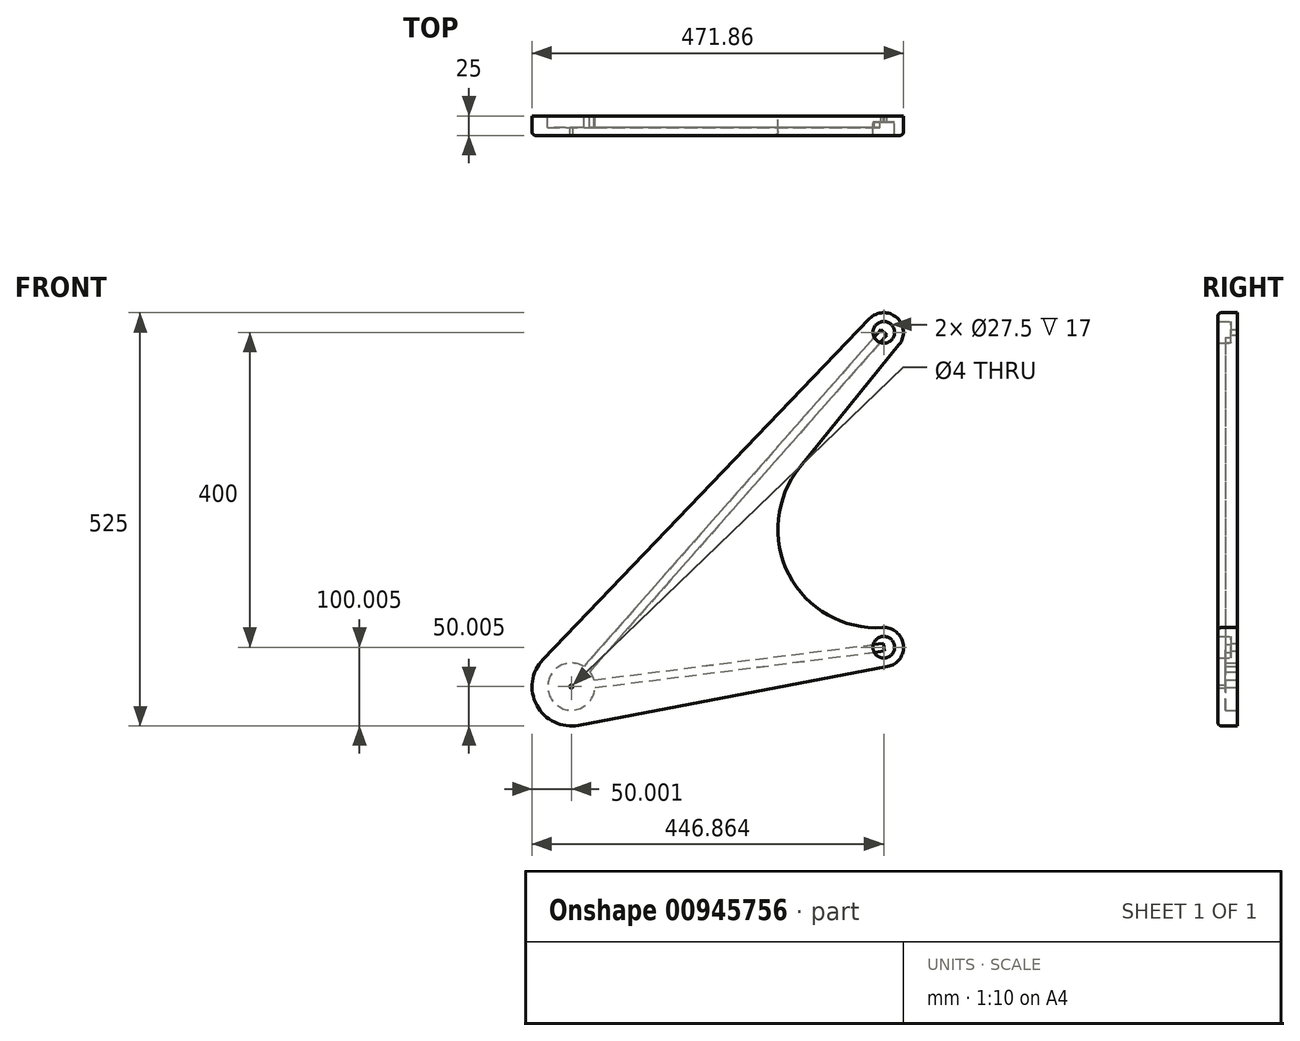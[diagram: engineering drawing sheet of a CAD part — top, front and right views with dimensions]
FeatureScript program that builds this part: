
annotation { "Feature Type Name" : "Feature", "Feature Type Description" : "" }
export const myFeature = defineFeature(function(context is Context, id is Id, definition is map)
    precondition{}
    {
        {
            var Q0;
            Q0=qCreatedBy(makeId("Front.planeOp"),FACE);
            var sketch = newSketch(context, id + "F0", { "sketchPlane" : qUnion([Q0])});
            skLineSegment(sketch, "E0", {"start": v(27.48, 326.53) * mm, "end": v(-369.38, -123.47) * mm});
            skLineSegment(sketch, "E1", {"start": v(-369.38, -123.47) * mm, "end": v(27.48, -73.47) * mm});
            skLineSegment(sketch, "E2", {"start": v(27.48, -73.47) * mm, "end": v(27.48, 326.53) * mm});
            skCircle(sketch, "E3", {"center": v(-369.38, -123.47) * mm, "radius": 50 * mm});
            skCircle(sketch, "E4", {"center": v(-369.38, -123.47) * mm, "radius": 30 * mm});
            skCircle(sketch, "E5", {"center": v(27.48, -73.47) * mm, "radius": 13.75 * mm});
            skCircle(sketch, "E6", {"center": v(27.48, 326.53) * mm, "radius": 13.75 * mm});
            skCircle(sketch, "E7", {"center": v(27.48, 326.53) * mm, "radius": 25 * mm});
            skCircle(sketch, "E8", {"center": v(27.48, -73.47) * mm, "radius": 25 * mm});
            skLineSegment(sketch, "E9", {"start": v(-405.47, -88.86) * mm, "end": v(9.44, 343.84) * mm});
            skLineSegment(sketch, "E10", {"start": v(-360.04, -172.59) * mm, "end": v(32.15, -98.03) * mm});
            skLineSegment(sketch, "E11", {"start": v(-330.53, -154.95) * mm, "end": v(46.9, 310.8) * mm});
            skLineSegment(sketch, "E12", {"start": v(25.92, -48.51) * mm, "end": v(-372.52, -73.56) * mm});
            skArc(sketch, "E13", {"start": v(25.92, -48.51) * mm, "mid": v(129.3, 133.79) * mm, "end": v(-79.18, 155.2) * mm});
            skCircle(sketch, "E14", {"center": v(18.06, 76.4) * mm, "radius": 125.17 * mm});
            skSolve(sketch);
        }
        {
            var Q0;
            {var subQ0=sQuery(id+"F0.wireOp",EDGE,"E3");var subQ2=sQuery(id+"F0.wireOp",EDGE,"E0");var subQ3=makeQuery(id+"F0.imprint","INTERSECT",VERTEX,{"derivedFrom":[subQ2,subQ0]});Q0=makeQuery(id+"F0.imprint","IMPRINT",FACE,{"disambiguationData":[TD([[makeQuery(id+"F0.imprint","IMPRINT",EDGE,{"disambiguationData":[TD([[subQ3,-1.0]])],"derivedFrom":subQ2}),-1.0]])]});}
            var Q1;
            {var subQ0=sQuery(id+"F0.wireOp",EDGE,"E3");var subQ1=sQuery(id+"F0.wireOp",EDGE,"E0");var subQ2=makeQuery(id+"F0.imprint","INTERSECT",VERTEX,{"derivedFrom":[subQ1,subQ0]});Q1=makeQuery(id+"F0.imprint","IMPRINT",FACE,{"disambiguationData":[TD([[makeQuery(id+"F0.imprint","IMPRINT",EDGE,{"disambiguationData":[TD([[subQ2,-1.0]])],"derivedFrom":subQ1}),1.0]])]});}
            var Q2;
            {var subQ0=sQuery(id+"F0.wireOp",EDGE,"E12");var subQ1=sQuery(id+"F0.wireOp",EDGE,"E0");var subQ2=makeQuery(id+"F0.imprint","INTERSECT",VERTEX,{"derivedFrom":[subQ1,subQ0]});Q2=makeQuery(id+"F0.imprint","IMPRINT",FACE,{"disambiguationData":[TD([[makeQuery(id+"F0.imprint","IMPRINT",EDGE,{"disambiguationData":[TD([[subQ2,-1.0]])],"derivedFrom":subQ1}),-1.0]])]});}
            var Q3;
            {var subQ0=sQuery(id+"F0.wireOp",EDGE,"E9");Q3=makeQuery(id+"F0.imprint","IMPRINT",FACE,{"disambiguationData":[TD([[makeQuery(id+"F0.imprint","IMPRINT",EDGE,{"derivedFrom":subQ0}),-1.0]])]});}
            var Q4;
            {var subQ4=sQuery(id+"F0.wireOp",EDGE,"E7");var subQ5=sQuery(id+"F0.wireOp",EDGE,"E0");var subQ6=makeQuery(id+"F0.imprint","INTERSECT",VERTEX,{"derivedFrom":[subQ5,subQ4]});Q4=makeQuery(id+"F0.imprint","IMPRINT",FACE,{"disambiguationData":[TD([[makeQuery(id+"F0.imprint","IMPRINT",EDGE,{"disambiguationData":[TD([[subQ6,-1.0]])],"derivedFrom":subQ5}),1.0]])]});}
            var Q5;
            {var subQ1=sQuery(id+"F0.wireOp",EDGE,"E0");var subQ7=sQuery(id+"F0.wireOp",EDGE,"E12");var subQ9=makeQuery(id+"F0.imprint","INTERSECT",VERTEX,{"derivedFrom":[subQ1,subQ7]});Q5=makeQuery(id+"F0.imprint","IMPRINT",FACE,{"disambiguationData":[TD([[makeQuery(id+"F0.imprint","IMPRINT",EDGE,{"disambiguationData":[TD([[subQ9,-1.0]])],"derivedFrom":subQ1}),1.0]])]});}
            var Q6;
            {var subQ0=sQuery(id+"F0.wireOp",EDGE,"E12");var subQ1=sQuery(id+"F0.wireOp",EDGE,"E11");var subQ2=makeQuery(id+"F0.imprint","INTERSECT",VERTEX,{"derivedFrom":[subQ1,subQ0]});Q6=makeQuery(id+"F0.imprint","IMPRINT",FACE,{"disambiguationData":[TD([[makeQuery(id+"F0.imprint","IMPRINT",EDGE,{"disambiguationData":[TD([[subQ2,-1.0]])],"derivedFrom":subQ1}),-1.0]])]});}
            var Q7;
            {var subQ1=sQuery(id+"F0.wireOp",EDGE,"E1");var subQ5=sQuery(id+"F0.wireOp",EDGE,"E8");var subQ7=makeQuery(id+"F0.imprint","INTERSECT",VERTEX,{"derivedFrom":[subQ1,subQ5]});Q7=makeQuery(id+"F0.imprint","IMPRINT",FACE,{"disambiguationData":[TD([[makeQuery(id+"F0.imprint","IMPRINT",EDGE,{"disambiguationData":[TD([[subQ7,-1.0]])],"derivedFrom":subQ1}),-1.0]])]});}
            var Q8;
            {var subQ0=sQuery(id+"F0.wireOp",EDGE,"E10");Q8=makeQuery(id+"F0.imprint","IMPRINT",FACE,{"disambiguationData":[TD([[makeQuery(id+"F0.imprint","IMPRINT",EDGE,{"derivedFrom":subQ0}),1.0]])]});}
            var Q9;
            {var subQ0=sQuery(id+"F0.wireOp",EDGE,"E8");var subQ5=sQuery(id+"F0.wireOp",EDGE,"E1");var subQ8=makeQuery(id+"F0.imprint","INTERSECT",VERTEX,{"derivedFrom":[subQ5,subQ0]});Q9=makeQuery(id+"F0.imprint","IMPRINT",FACE,{"disambiguationData":[TD([[makeQuery(id+"F0.imprint","IMPRINT",EDGE,{"disambiguationData":[TD([[subQ8,-1.0]])],"derivedFrom":subQ5}),1.0]])]});}
            var Q10;
            {var subQ0=sQuery(id+"F0.wireOp",EDGE,"E11");var subQ1=sQuery(id+"F0.wireOp",EDGE,"E1");var subQ2=makeQuery(id+"F0.imprint","INTERSECT",VERTEX,{"derivedFrom":[subQ1,subQ0]});Q10=makeQuery(id+"F0.imprint","IMPRINT",FACE,{"disambiguationData":[TD([[makeQuery(id+"F0.imprint","IMPRINT",EDGE,{"disambiguationData":[TD([[subQ2,-1.0]])],"derivedFrom":subQ1}),1.0]])]});}
            var Q11;
            {var subQ0=sQuery(id+"F0.wireOp",EDGE,"E3");var subQ1=sQuery(id+"F0.wireOp",EDGE,"E1");var subQ2=makeQuery(id+"F0.imprint","INTERSECT",VERTEX,{"derivedFrom":[subQ1,subQ0]});Q11=makeQuery(id+"F0.imprint","IMPRINT",FACE,{"disambiguationData":[TD([[makeQuery(id+"F0.imprint","IMPRINT",EDGE,{"disambiguationData":[TD([[subQ2,-1.0]])],"derivedFrom":subQ1}),-1.0]])]});}
            var Q12;
            {var subQ0=sQuery(id+"F0.wireOp",EDGE,"E11");var subQ1=sQuery(id+"F0.wireOp",EDGE,"E2");var subQ2=makeQuery(id+"F0.imprint","INTERSECT",VERTEX,{"derivedFrom":[subQ1,subQ0]});Q12=makeQuery(id+"F0.imprint","IMPRINT",FACE,{"disambiguationData":[TD([[makeQuery(id+"F0.imprint","IMPRINT",EDGE,{"disambiguationData":[TD([[subQ2,-1.0]])],"derivedFrom":subQ1}),-1.0]])]});}
            var Q13;
            {var subQ2=sQuery(id+"F0.wireOp",EDGE,"E0");var subQ6=sQuery(id+"F0.wireOp",EDGE,"E6");var subQ8=makeQuery(id+"F0.imprint","INTERSECT",VERTEX,{"derivedFrom":[subQ2,subQ6]});Q13=makeQuery(id+"F0.imprint","IMPRINT",FACE,{"disambiguationData":[TD([[makeQuery(id+"F0.imprint","IMPRINT",EDGE,{"disambiguationData":[TD([[subQ8,-1.0]])],"derivedFrom":subQ2}),-1.0]])]});}
            var Q14;
            {var subQ0=sQuery(id+"F0.wireOp",EDGE,"E6");var subQ1=sQuery(id+"F0.wireOp",EDGE,"E0");var subQ2=makeQuery(id+"F0.imprint","INTERSECT",VERTEX,{"derivedFrom":[subQ1,subQ0]});Q14=makeQuery(id+"F0.imprint","IMPRINT",FACE,{"disambiguationData":[TD([[makeQuery(id+"F0.imprint","IMPRINT",EDGE,{"disambiguationData":[TD([[subQ2,-1.0]])],"derivedFrom":subQ1}),1.0]])]});}
            extrude(context, id + "F1", {"entities" : qUnion([Q0, Q1, Q2, Q3, Q4, Q5, Q6, Q7, Q8, Q9, Q10, Q11, Q12, Q13, Q14]), "depth" : 25 * mm, "offsetDistance" : 25 * mm});
        }
        {
            var Q0;
            {var subQ0=sQuery(id+"F0.wireOp",EDGE,"E2");var subQ1=sQuery(id+"F0.wireOp",EDGE,"E1");var subQ2=makeQuery(id+"F0.imprint","INTERSECT",VERTEX,{"derivedFrom":[subQ1,subQ0]});Q0=makeQuery(id+"F0.imprint","IMPRINT",FACE,{"disambiguationData":[TD([[makeQuery(id+"F0.imprint","IMPRINT",EDGE,{"disambiguationData":[TD([[subQ2,1.0]])],"derivedFrom":subQ1}),1.0]])]});}
            var Q1;
            {var subQ0=sQuery(id+"F0.wireOp",EDGE,"E2");var subQ1=sQuery(id+"F0.wireOp",EDGE,"E1");var subQ2=makeQuery(id+"F0.imprint","INTERSECT",VERTEX,{"derivedFrom":[subQ1,subQ0]});Q1=makeQuery(id+"F0.imprint","IMPRINT",FACE,{"disambiguationData":[TD([[makeQuery(id+"F0.imprint","IMPRINT",EDGE,{"disambiguationData":[TD([[subQ2,1.0]])],"derivedFrom":subQ1}),-1.0]])]});}
            var Q2;
            {var subQ0=sQuery(id+"F0.wireOp",EDGE,"E2");var subQ1=sQuery(id+"F0.wireOp",EDGE,"E0");var subQ2=makeQuery(id+"F0.imprint","INTERSECT",VERTEX,{"derivedFrom":[subQ1,subQ0]});Q2=makeQuery(id+"F0.imprint","IMPRINT",FACE,{"disambiguationData":[TD([[makeQuery(id+"F0.imprint","IMPRINT",EDGE,{"disambiguationData":[TD([[subQ2,-1.0]])],"derivedFrom":subQ1}),1.0]])]});}
            var Q3;
            {var subQ0=sQuery(id+"F0.wireOp",EDGE,"E2");var subQ1=sQuery(id+"F0.wireOp",EDGE,"E0");var subQ2=makeQuery(id+"F0.imprint","INTERSECT",VERTEX,{"derivedFrom":[subQ1,subQ0]});Q3=makeQuery(id+"F0.imprint","IMPRINT",FACE,{"disambiguationData":[TD([[makeQuery(id+"F0.imprint","IMPRINT",EDGE,{"disambiguationData":[TD([[subQ2,-1.0]])],"derivedFrom":subQ1}),-1.0]])]});}
            extrude(context, id + "F2", {"entities" : qUnion([Q0, Q1, Q2, Q3]), "operationType" : NewBodyOperationType.ADD, "depth" : 8 * mm, "offsetDistance" : 25 * mm});
        }
        {
            var Q0;
            {var subQ0=sQuery(id+"F0.wireOp",EDGE,"E1");var subQ1=sQuery(id+"F0.wireOp",EDGE,"E0");var subQ2=makeQuery(id+"F0.imprint","INTERSECT",VERTEX,{"derivedFrom":[subQ1,subQ0]});Q0=makeQuery(id+"F0.imprint","IMPRINT",FACE,{"disambiguationData":[TD([[makeQuery(id+"F0.imprint","IMPRINT",EDGE,{"disambiguationData":[TD([[subQ2,1.0]])],"derivedFrom":subQ1}),-1.0]])]});}
            var Q1;
            {var subQ0=sQuery(id+"F0.wireOp",EDGE,"E1");var subQ1=sQuery(id+"F0.wireOp",EDGE,"E0");var subQ2=makeQuery(id+"F0.imprint","INTERSECT",VERTEX,{"derivedFrom":[subQ1,subQ0]});Q1=makeQuery(id+"F0.imprint","IMPRINT",FACE,{"disambiguationData":[TD([[makeQuery(id+"F0.imprint","IMPRINT",EDGE,{"disambiguationData":[TD([[subQ2,1.0]])],"derivedFrom":subQ1}),1.0]])]});}
            extrude(context, id + "F3", {"entities" : qUnion([Q0, Q1]), "operationType" : NewBodyOperationType.ADD, "depth" : 25 * mm, "offsetDistance" : 25 * mm});
        }
        {
            var Q0;
            {var subQ0=sQuery(id+"F0.wireOp",EDGE,"E1");var subQ1=sQuery(id+"F0.wireOp",EDGE,"E0");var subQ2=makeQuery(id+"F0.imprint","INTERSECT",VERTEX,{"derivedFrom":[subQ1,subQ0]});Q0=makeQuery(id+"F0.imprint","IMPRINT",FACE,{"disambiguationData":[TD([[makeQuery(id+"F0.imprint","IMPRINT",EDGE,{"disambiguationData":[TD([[subQ2,1.0]])],"derivedFrom":subQ1}),1.0]])]});}
            var Q1;
            {var subQ0=sQuery(id+"F0.wireOp",EDGE,"E1");var subQ1=sQuery(id+"F0.wireOp",EDGE,"E0");var subQ2=makeQuery(id+"F0.imprint","INTERSECT",VERTEX,{"derivedFrom":[subQ1,subQ0]});Q1=makeQuery(id+"F0.imprint","IMPRINT",FACE,{"disambiguationData":[TD([[makeQuery(id+"F0.imprint","IMPRINT",EDGE,{"disambiguationData":[TD([[subQ2,1.0]])],"derivedFrom":subQ1}),-1.0]])]});}
            extrude(context, id + "F4", {"entities" : qUnion([Q0, Q1]), "operationType" : NewBodyOperationType.REMOVE, "depth" : 15 * mm, "offsetDistance" : 25 * mm});
        }
        {
            var Q0;
            Q0=qCreatedBy(makeId("Front.planeOp"),FACE);
            var sketch = newSketch(context, id + "F5", { "sketchPlane" : qUnion([Q0])});
            skLineSegment(sketch, "E15.0", {"start": v(-368.75, -128.43) * mm, "end": v(28.1, -78.43) * mm});
            skLineSegment(sketch, "E16.0", {"start": v(-370, -118.5) * mm, "end": v(26.86, -68.5) * mm});
            skLineSegment(sketch, "E17", {"start": v(-368.75, -128.43) * mm, "end": v(-370, -118.5) * mm});
            skLineSegment(sketch, "E18", {"start": v(28.1, -78.43) * mm, "end": v(26.86, -68.5) * mm});
            skLineSegment(sketch, "E19.0", {"start": v(23.73, 329.84) * mm, "end": v(-373.13, -120.16) * mm});
            skLineSegment(sketch, "E20.0", {"start": v(31.23, 323.23) * mm, "end": v(-365.63, -126.77) * mm});
            skLineSegment(sketch, "E21", {"start": v(-373.13, -120.16) * mm, "end": v(-365.63, -126.77) * mm});
            skLineSegment(sketch, "E22", {"start": v(23.73, 329.84) * mm, "end": v(31.23, 323.23) * mm});
            skSolve(sketch);
        }
        {
            var Q0;
            {var subQ1=sQuery(id+"F5.wireOp",EDGE,"E15.0");Q0=makeQuery(id+"F5.imprint","IMPRINT",FACE,{"disambiguationData":[TD([[makeQuery(id+"F5.imprint","IMPRINT",EDGE,{"derivedFrom":subQ1}),1.0]])]});}
            var Q1;
            {var subQ8=sQuery(id+"F5.wireOp",EDGE,"E19.0");Q1=makeQuery(id+"F5.imprint","IMPRINT",FACE,{"disambiguationData":[TD([[makeQuery(id+"F5.imprint","IMPRINT",EDGE,{"derivedFrom":subQ8}),1.0]])]});}
            extrude(context, id + "F6", {"entities" : qUnion([Q0, Q1]), "operationType" : NewBodyOperationType.REMOVE, "depth" : 15 * mm, "offsetDistance" : 25 * mm});
        }
        {
            var Q0;
            Q0=sQuery(id+"F0.wireOp",VERTEX,"E0.end");
            var Q1;
            Q1=makeQuery(id+"F1.opExtrude","SWEPT_BODY",BODY,{"disambiguationData":[OSD([sQuery(id+"F0.wireOp",EDGE,"E3"),sQuery(id+"F0.wireOp",EDGE,"E4"),sQuery(id+"F0.wireOp",EDGE,"E5"),sQuery(id+"F0.wireOp",EDGE,"E6"),sQuery(id+"F0.wireOp",EDGE,"E7"),sQuery(id+"F0.wireOp",EDGE,"E8"),sQuery(id+"F0.wireOp",EDGE,"E9"),sQuery(id+"F0.wireOp",EDGE,"E10"),sQuery(id+"F0.wireOp",EDGE,"E11"),sQuery(id+"F0.wireOp",EDGE,"E14")])]});
            hole(context, id + "F7", {"style" : HoleStyle.SIMPLE, "endStyle" : HoleEndStyle.THROUGH, "oppositeDirection" : true, "holeDiameter" : 4 * mm, "majorDiameter" : 5 * mm, "isTappedThrough" : true, "tappedDepth" : 12 * mm, "tapClearance" : 3, "locations" : qUnion([Q0]), "scope" : qUnion([Q1])});
        }
        {
            var Q0;
            Q0=makeQuery(id+"F1.opExtrude","CAP_EDGE",EDGE,{"disambiguationData":[OSD([sQuery(id+"F0.wireOp",EDGE,"E9")])],"isStart":false});
            fillet(context, id + "F8", {"entities" : qUnion([Q0]), "radius" : 5 * mm, "tangentPropagation" : true, "allowEdgeOverflow" : false});
        }
    });
